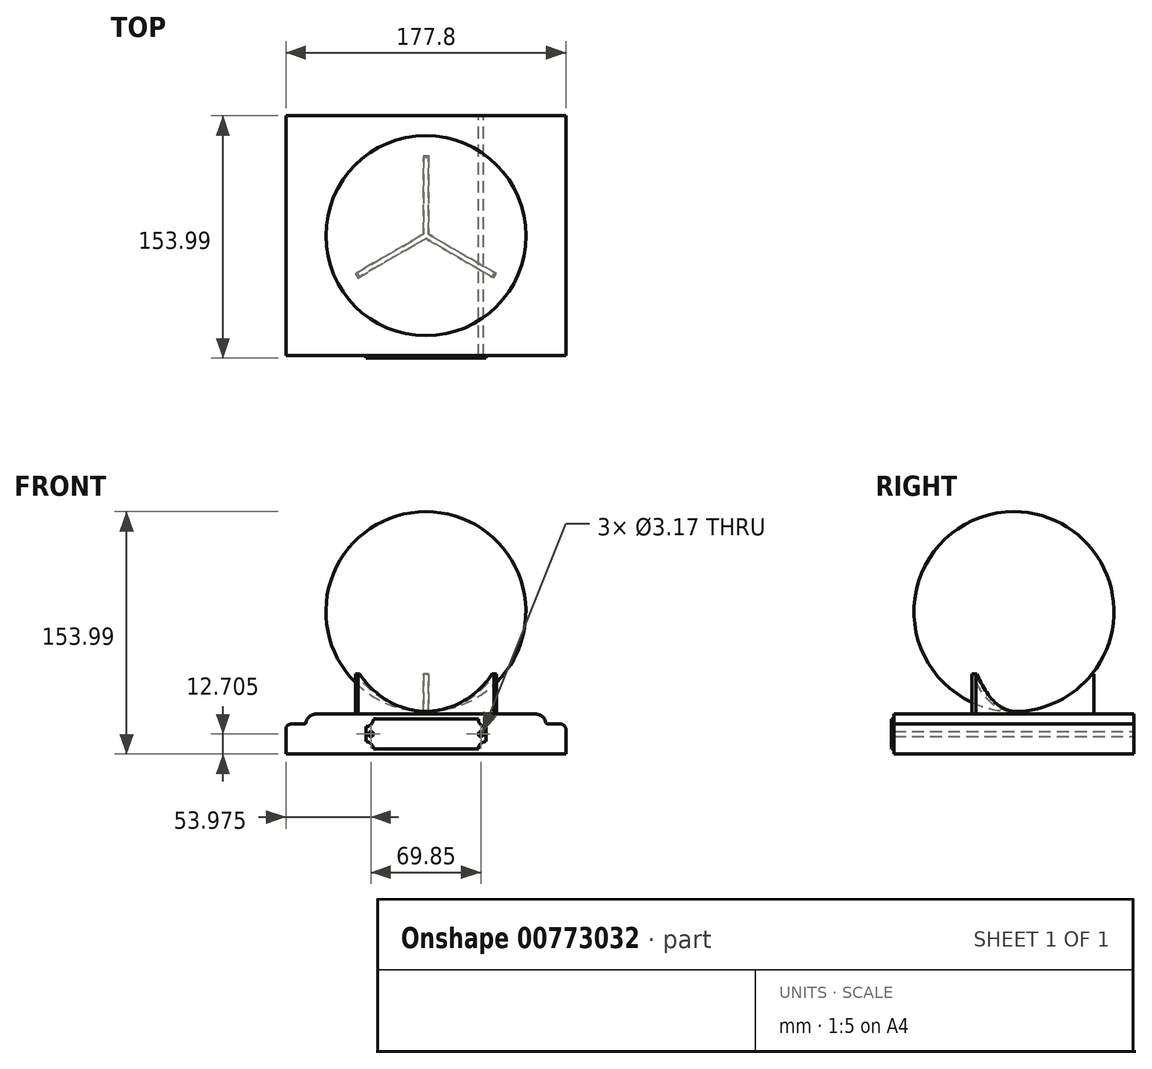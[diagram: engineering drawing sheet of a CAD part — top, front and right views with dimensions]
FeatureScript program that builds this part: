
annotation { "Feature Type Name" : "Feature", "Feature Type Description" : "" }
export const myFeature = defineFeature(function(context is Context, id is Id, definition is map)
    precondition{}
    {
        {
            var Q0;
            Q0=qCreatedBy(makeId("Front.planeOp"),FACE);
            var sketch = newSketch(context, id + "F0", { "sketchPlane" : qUnion([Q0])});
            skLineSegment(sketch, "E0.bottom", {"start": v(-85.73, 9.53) * mm, "end": v(-77.63, 9.53) * mm});
            skLineSegment(sketch, "E0.top", {"start": v(-88.9, -9.53) * mm, "end": v(88.9, -9.53) * mm});
            skLineSegment(sketch, "E0.left", {"start": v(-88.9, 6.35) * mm, "end": v(-88.9, -9.52) * mm});
            skLineSegment(sketch, "E0.right", {"start": v(88.9, 6.35) * mm, "end": v(88.9, -9.52) * mm});
            skPoint(sketch, "E0.middle", {"position": v(0, 0) * mm});
            skLineSegment(sketch, "E1.top", {"start": v(-69.85, 15.88) * mm, "end": v(69.85, 15.88) * mm});
            skLineSegment(sketch, "E1.left", {"start": v(-76.2, 10.42) * mm, "end": v(-76.2, 12.7) * mm});
            skLineSegment(sketch, "E1.right", {"start": v(76.2, 9.53) * mm, "end": v(76.2, 9.52) * mm});
            skPoint(sketch, "E1.middle", {"position": v(0, 12.7) * mm});
            skPoint(sketch, "E2.visualSharp", {"position": v(-76.2, 15.88) * mm});
            skArc(sketch, "E2.filletArc", {"start": v(-69.85, 15.88) * mm, "mid": v(-73.87, 14.44) * mm, "end": v(-76.07, 10.8) * mm});
            skPoint(sketch, "E3.visualSharp", {"position": v(76.2, 15.88) * mm});
            skArc(sketch, "E3.filletArc", {"start": v(76.07, 10.8) * mm, "mid": v(73.87, 14.44) * mm, "end": v(69.85, 15.88) * mm});
            skLineSegment(sketch, "E4.bottom", {"start": v(-33.34, 12.7) * mm, "end": v(33.34, 12.7) * mm});
            skLineSegment(sketch, "E4.top", {"start": v(-33.34, -6.35) * mm, "end": v(33.34, -6.35) * mm});
            skLineSegment(sketch, "E4.left", {"start": v(-38.1, 7.94) * mm, "end": v(-38.1, -1.59) * mm});
            skLineSegment(sketch, "E4.right", {"start": v(38.1, 7.94) * mm, "end": v(38.1, -1.59) * mm});
            skPoint(sketch, "E4.middle", {"position": v(0, 3.17) * mm});
            skArc(sketch, "E5", {"start": v(33.34, 12.7) * mm, "mid": v(34.73, 9.33) * mm, "end": v(38.1, 7.94) * mm});
            skArc(sketch, "E6", {"start": v(38.1, -1.59) * mm, "mid": v(34.73, -2.98) * mm, "end": v(33.34, -6.35) * mm});
            skArc(sketch, "E7", {"start": v(-33.34, -6.35) * mm, "mid": v(-34.73, -2.98) * mm, "end": v(-38.1, -1.59) * mm});
            skArc(sketch, "E8", {"start": v(-38.1, 7.94) * mm, "mid": v(-34.73, 9.33) * mm, "end": v(-33.34, 12.7) * mm});
            skCircle(sketch, "E9", {"center": v(-34.93, 3.17) * mm, "radius": 1.59 * mm});
            skPoint(sketch, "E9.centerSnap0", {"position": v(-38.1, 3.17) * mm});
            skCircle(sketch, "E10.MirrorC", {"center": v(34.93, 3.17) * mm, "radius": 1.59 * mm});
            skPoint(sketch, "E11.newPointA", {"position": v(88.9, 9.53) * mm});
            skArc(sketch, "E11.filletArc", {"start": v(-77.63, 9.53) * mm, "mid": v(-76.62, 9.88) * mm, "end": v(-76.07, 10.8) * mm});
            skArc(sketch, "E12.MirrorCS", {"start": v(77.63, 9.53) * mm, "mid": v(76.62, 9.88) * mm, "end": v(76.07, 10.8) * mm});
            skLineSegment(sketch, "E13.MirrorCS", {"start": v(85.73, 9.53) * mm, "end": v(77.63, 9.53) * mm});
            skPoint(sketch, "E14.visualSharp", {"position": v(-88.9, 9.53) * mm});
            skArc(sketch, "E14.filletArc", {"start": v(-85.73, 9.52) * mm, "mid": v(-87.97, 8.6) * mm, "end": v(-88.9, 6.35) * mm});
            skArc(sketch, "E15.filletArc", {"start": v(88.9, 6.35) * mm, "mid": v(87.97, 8.6) * mm, "end": v(85.73, 9.53) * mm});
            skLineSegment(sketch, "E16", {"start": v(0, 15.88) * mm, "end": v(0, -9.53) * mm, "construction": true});
            skPoint(sketch, "E17.orphan", {"position": v(-76.2, 9.53) * mm});
            skSolve(sketch);
        }
        {
            var Q0;
            Q0 = qSketchRegion(id + "F0", true);
            var Q1;
            Q1=makeQuery(id+"F0.imprint","IMPRINT",FACE,{"disambiguationData":[TD([[makeQuery(id+"F0.imprint","IMPRINT",EDGE,{"derivedFrom":sQuery(id+"F0.wireOp",EDGE,"E4.bottom")}),-1.0]])]});
            var Q2;
            Q2=makeQuery(id+"F0.imprint","IMPRINT",FACE,{"disambiguationData":[TD([[makeQuery(id+"F0.imprint","IMPRINT",EDGE,{"derivedFrom":sQuery(id+"F0.wireOp",EDGE,"E9")}),1.0]])]});
            var Q3;
            Q3=makeQuery(id+"F0.imprint","IMPRINT",FACE,{"disambiguationData":[TD([[makeQuery(id+"F0.imprint","IMPRINT",EDGE,{"derivedFrom":sQuery(id+"F0.wireOp",EDGE,"E10.MirrorC")}),-1.0]])]});
            extrude(context, id + "F1", {"entities" : qUnion([Q0, Q1, Q2, Q3]), "endBound" : BoundingType.SYMMETRIC, "depth" : 152.4 * mm, "offsetDistance" : 25.4 * mm});
        }
        {
            var Q0;
            Q0=makeQuery(id+"F1.opExtrude","SWEPT_FACE",FACE,{"disambiguationData":[OSD([sQuery(id+"F0.wireOp",EDGE,"E1.top")])]});
            var sketch = newSketch(context, id + "F2", { "sketchPlane" : qUnion([Q0])});
            skCircle(sketch, "E18", {"center": v(0, 0) * mm, "radius": 50.8 * mm});
            skLineSegment(sketch, "E19", {"start": v(0, 0) * mm, "end": v(0, 50.8) * mm, "construction": true});
            skLineSegment(sketch, "E20.1.0", {"start": v(0, 0) * mm, "end": v(-44, -25.4) * mm, "construction": true});
            skLineSegment(sketch, "E20.2.0", {"start": v(0, 0) * mm, "end": v(44, -25.4) * mm, "construction": true});
            skLineSegment(sketch, "E21.bottom", {"start": v(-1.59, 50.78) * mm, "end": v(1.59, 50.78) * mm});
            skLineSegment(sketch, "E21.top", {"start": v(-1.59, 0.02) * mm, "end": v(1.59, 0.02) * mm});
            skLineSegment(sketch, "E21.left", {"start": v(-1.59, 50.78) * mm, "end": v(-1.59, 0.02) * mm});
            skLineSegment(sketch, "E21.right", {"start": v(1.59, 50.78) * mm, "end": v(1.59, 0.02) * mm});
            skPoint(sketch, "E21.middle", {"position": v(0, 25.4) * mm});
            skLineSegment(sketch, "E22.1.0", {"start": v(-44.77, -24.01) * mm, "end": v(-0.82, 1.36) * mm});
            skLineSegment(sketch, "E22.1.1", {"start": v(-43.18, -26.76) * mm, "end": v(0.77, -1.39) * mm});
            skLineSegment(sketch, "E22.2.0", {"start": v(43.18, -26.76) * mm, "end": v(-0.77, -1.39) * mm});
            skLineSegment(sketch, "E22.2.1", {"start": v(44.77, -24.01) * mm, "end": v(0.82, 1.36) * mm});
            skSolve(sketch);
        }
        {
            var Q0;
            {var subQ3=sQuery(id+"F2.wireOp",EDGE,"E21.bottom");Q0=makeQuery(id+"F2.imprint","IMPRINT",FACE,{"disambiguationData":[TD([[makeQuery(id+"F2.imprint","IMPRINT",EDGE,{"derivedFrom":subQ3}),-1.0]])]});}
            var Q1;
            {var subQ1=sQuery(id+"F2.wireOp",EDGE,"E21.top");Q1=makeQuery(id+"F2.imprint","IMPRINT",FACE,{"disambiguationData":[TD([[makeQuery(id+"F2.imprint","IMPRINT",EDGE,{"derivedFrom":subQ1}),-1.0]])]});}
            extrude(context, id + "F3", {"entities" : qUnion([Q0, Q1]), "depth" : 25.4 * mm, "offsetDistance" : 25.4 * mm});
        }
        {
            var Q0;
            Q0=qCreatedBy(makeId("Front.planeOp"),FACE);
            var sketch = newSketch(context, id + "F4", { "sketchPlane" : qUnion([Q0])});
            skCircle(sketch, "E23", {"center": v(0, 80.96) * mm, "radius": 63.5 * mm});
            skLineSegment(sketch, "E24", {"start": v(0, 144.46) * mm, "end": v(0, 17.46) * mm});
            skSolve(sketch);
        }
        {
            var Q0;
            {var subQ0=sQuery(id+"F4.wireOp",EDGE,"E24");Q0=makeQuery(id+"F4.imprint","IMPRINT",FACE,{"disambiguationData":[TD([[makeQuery(id+"F4.imprint","IMPRINT",EDGE,{"derivedFrom":subQ0}),1.0]])]});}
            var Q1;
            Q1=sQuery(id+"F4.wireOp",EDGE,"E24");
            revolve(context, id + "F5", {"surfaceOperationType" : NewSurfaceOperationType.NEW, "entities" : qUnion([Q0]), "axis" : qUnion([Q1]), "revolveType" : RevolveType.FULL});
        }
        {
            var Q0;
            Q0=makeQuery(id+"F5.opRevolve","SWEPT_BODY",BODY,{"disambiguationData":[OSD([sQuery(id+"F4.wireOp",EDGE,"E23"),sQuery(id+"F4.wireOp",EDGE,"E24")])]});
            var Q1;
            Q1=makeQuery(id+"F3.opExtrude","SWEPT_BODY",BODY,{"disambiguationData":[OSD([sQuery(id+"F2.wireOp",EDGE,"E18"),sQuery(id+"F2.wireOp",EDGE,"E21.bottom"),sQuery(id+"F2.wireOp",EDGE,"E21.left"),sQuery(id+"F2.wireOp",EDGE,"E21.right"),sQuery(id+"F2.wireOp",EDGE,"E22.1.0"),sQuery(id+"F2.wireOp",EDGE,"E22.1.1"),sQuery(id+"F2.wireOp",EDGE,"E22.2.0"),sQuery(id+"F2.wireOp",EDGE,"E22.2.1")])]});
            booleanBodies(context, id + "F6", {"operationType" : BooleanOperationType.SUBTRACTION, "tools" : qUnion([Q0]), "targets" : qUnion([Q1]), "keepTools" : true});
        }
        {
            var Q0;
            Q0=makeQuery(id+"F1.opExtrude","CAP_FACE",FACE,{"disambiguationData":[OSD([sQuery(id+"F0.wireOp",EDGE,"E0.bottom"),sQuery(id+"F0.wireOp",EDGE,"E0.top"),sQuery(id+"F0.wireOp",EDGE,"E0.left"),sQuery(id+"F0.wireOp",EDGE,"E0.right"),sQuery(id+"F0.wireOp",EDGE,"E1.top"),sQuery(id+"F0.wireOp",EDGE,"E2.filletArc"),sQuery(id+"F0.wireOp",EDGE,"E3.filletArc"),sQuery(id+"F0.wireOp",EDGE,"E11.filletArc"),sQuery(id+"F0.wireOp",EDGE,"E12.MirrorCS"),sQuery(id+"F0.wireOp",EDGE,"E13.MirrorCS"),sQuery(id+"F0.wireOp",EDGE,"E14.filletArc"),sQuery(id+"F0.wireOp",EDGE,"E15.filletArc")])],"isStart":false});
            var sketch = newSketch(context, id + "F7", { "sketchPlane" : qUnion([Q0])});
            skLineSegment(sketch, "E25.0", {"start": v(-33.34, 12.7) * mm, "end": v(33.34, 12.7) * mm});
            skArc(sketch, "E25.1", {"start": v(-38.1, 7.94) * mm, "mid": v(-34.73, 9.33) * mm, "end": v(-33.34, 12.7) * mm});
            skLineSegment(sketch, "E25.2", {"start": v(-38.1, 7.94) * mm, "end": v(-38.1, -1.59) * mm});
            skCircle(sketch, "E25.3", {"center": v(-34.93, 3.17) * mm, "radius": 1.59 * mm});
            skArc(sketch, "E25.4", {"start": v(-33.34, -6.35) * mm, "mid": v(-34.73, -2.98) * mm, "end": v(-38.1, -1.59) * mm});
            skLineSegment(sketch, "E25.5", {"start": v(-33.34, -6.35) * mm, "end": v(33.34, -6.35) * mm});
            skArc(sketch, "E25.6", {"start": v(38.1, -1.59) * mm, "mid": v(34.73, -2.98) * mm, "end": v(33.34, -6.35) * mm});
            skLineSegment(sketch, "E25.7", {"start": v(38.1, 7.94) * mm, "end": v(38.1, -1.59) * mm});
            skArc(sketch, "E25.8", {"start": v(33.34, 12.7) * mm, "mid": v(34.73, 9.33) * mm, "end": v(38.1, 7.94) * mm});
            skCircle(sketch, "E25.9", {"center": v(34.93, 3.17) * mm, "radius": 1.59 * mm});
            skSolve(sketch);
        }
        {
            var Q0;
            Q0 = qSketchRegion(id + "F7", true);
            extrude(context, id + "F8", {"entities" : qUnion([Q0]), "depth" : 1.59 * mm, "offsetDistance" : 25.4 * mm});
        }
    });
